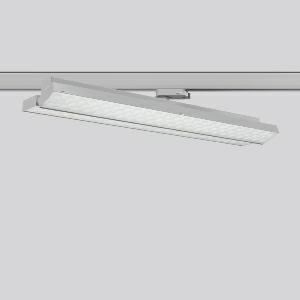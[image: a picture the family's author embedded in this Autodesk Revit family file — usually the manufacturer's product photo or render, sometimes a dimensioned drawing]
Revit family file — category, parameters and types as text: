
# Revit family: tx-move_742161_004_2_76_01f6
name_source: partatom
category: Lighting Fixtures
units: mm (PartAtom-declared; Revit-internal decimal feet)

## family parameters
Cut with Voids When Loaded = No
Host = Face
Light Source = No
Part Type = Normal
Room Calculation Point = No
Round Connector Dimension = Use Diameter
Shared = No

## types (1)
- MultiLumen 1 (1 x LED Modul 927, 2100 lm, 2700)
    Apparent Load = 38 VA
    CIE Flux Codes = 90 97 99 100 100
    Color Rendering = 92
    Color Temperature = 2700
    Default Elevation = 1800 mm
    Description = Series: TX-MOVE
Multifunctional surface-mounted spotlight for area lighting. Very flat design. Housing: sheet steel, powder-coated. Rotation range: 356°. Swivel range: 90°. Consistent alignment possible with visible tilt scale. High-efficiency LED units with optimum light control thanks to clear plastic (PC) lens optics. Spezielle Mikrostrukturen reduzieren Gelbsaum. Symmetrical light distribution. Best colour rendering with CRI >90 for fresh products and coloured textiles. With adapter for RZB 3-circuit DALI tracks. Suitable for Track on ceiling. MultiLumen: Luminous flux adjustable in 3 steps. Factory setting is the highest luminous flux. Environmentally friendly and resource-saving due to replaceable and recyclable components. Very good glare control, ideal for till areas. 
Colour: silver, matt (approx. RAL 9006)
Length: 570 mm
Width: 119 mm
Height: 88 mm
Lamp: LED
Socket: without socket
Colour temperature: 2700K
Colour rendering index (CRI): 90
System power: 38 W
Rated luminous flux: 4200 lm
Luminous efficiency: 111 lm/W
System power 2: 51 W
Rated luminous flux 2: 5500 lm
Luminous efficiency 2: 108 lm/W
System power 3: 62 W
Rated luminous flux 3: 6500 lm
Luminous efficiency 3: 105 lm/W
Control gear: Dimmable EVG, DALI
Protection class: I
Type of protection: IP 20
    Height = 75 mm
    Lamp = 1 x LED Modul 927
    Lamp Light Flux = 2100 lm
    Lamp count = 1
    Length = 569 mm
    Lifetime = 50000 h
    Luminous efficacy = 111 lm/W
    Manufacturer = RZB
    ModVariant = No
    Model = 742161.004.2.76
    Mounting Place = Ceiling
    Mounting Type = Surface mounted
    Number of Poles = 1
    OnlyDefault = Yes
    Power Factor = 1
    Product Name = TX-MOVE
    Product group = Track mounted projectors
    ProductGroupID = 301
    Protection Class = Protection class I
    Protection Degree = IP 20
    RLX_Detail_Level = 1
    RLX_Emergency_Light_Flux = 0 lm
    RLX_Emergency_Type = 0
    RLX_Emergency_Type_DB = No
    RlxData = <blob elided: 33365 chars, md5=80a922d5>
    Socket = socket
    Standby Power = 0 W
    System Light Flux = 4200 lm
    System Power = 38 W
    Type Comments = MultiLumen 1
    Type Image = 742162.004.jpg
    URL = http://relux.com
    VarID = multilumen_1
    Voltage = 0 V
    Weight = 0.00 kg
    Width = 119 mm

## geometry (parser evidence)
native form markers: Blend x4, Sweep x16
no freeform markers — native parametric forms only
